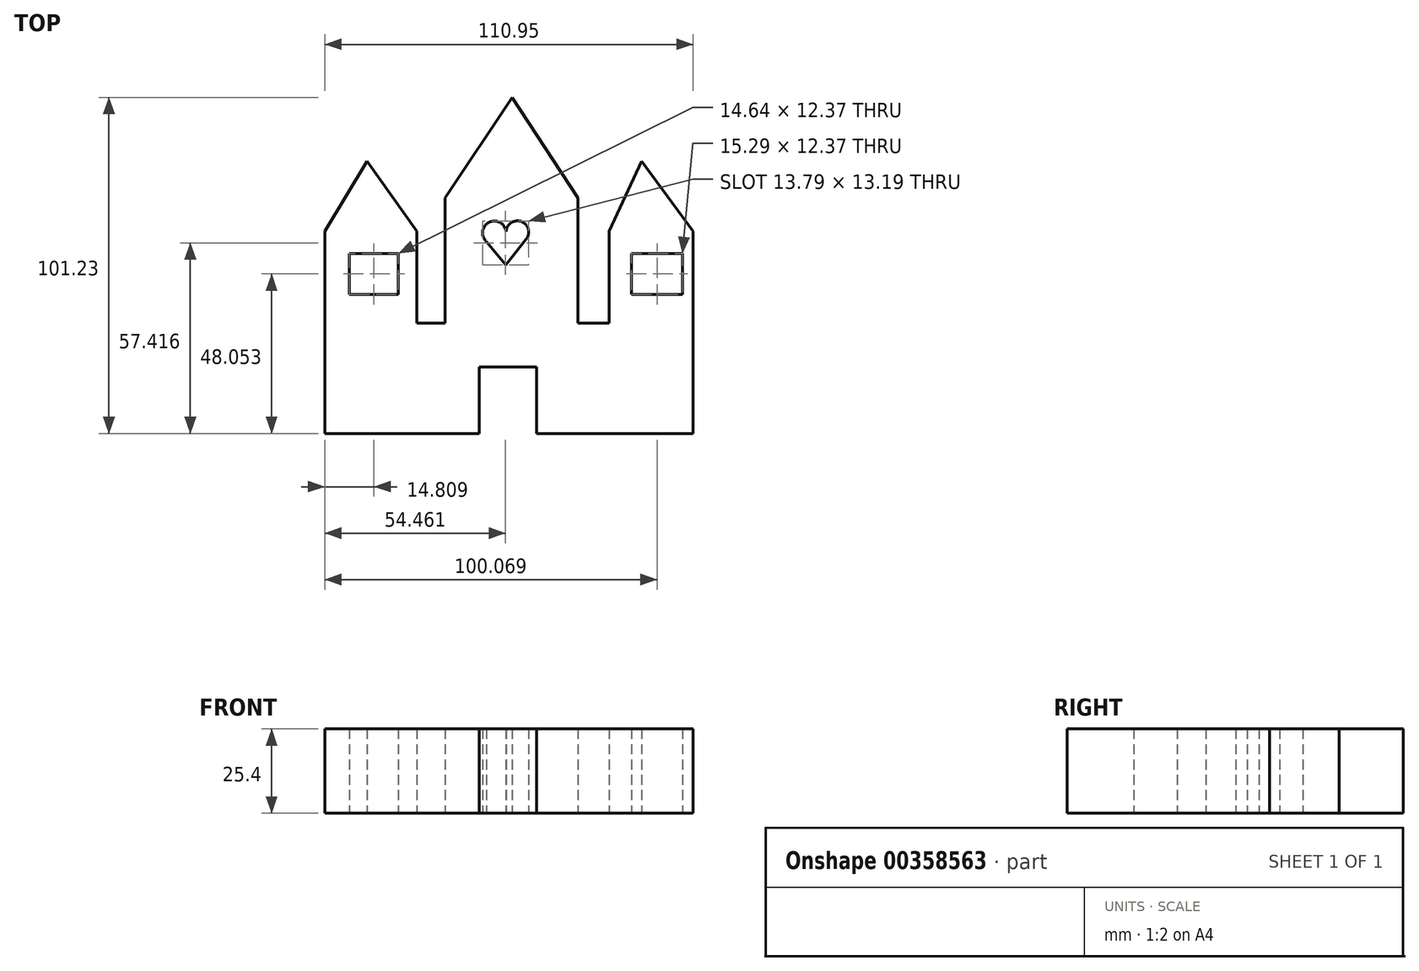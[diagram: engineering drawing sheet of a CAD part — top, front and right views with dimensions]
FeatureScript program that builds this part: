
annotation { "Feature Type Name" : "Feature", "Feature Type Description" : "" }
export const myFeature = defineFeature(function(context is Context, id is Id, definition is map)
    precondition{}
    {
        {
            var Q0;
            Q0=qCreatedBy(makeId("Top.planeOp"),FACE);
            var sketch = newSketch(context, id + "F0", { "sketchPlane" : qUnion([Q0])});
            skLineSegment(sketch, "E0.bottom", {"start": v(-8.53, -12.04) * mm, "end": v(0, -12.04) * mm});
            skLineSegment(sketch, "E0.top", {"start": v(-36.27, -45.26) * mm, "end": v(74.68, -45.26) * mm});
            skLineSegment(sketch, "E0.left", {"start": v(-36.27, -12.04) * mm, "end": v(-36.27, -45.26) * mm});
            skLineSegment(sketch, "E0.right", {"start": v(74.68, -12.04) * mm, "end": v(74.68, -45.26) * mm});
            skLineSegment(sketch, "E1", {"start": v(-36.27, -12.04) * mm, "end": v(-36.27, 15.7) * mm});
            skLineSegment(sketch, "E2", {"start": v(-8.53, -12.04) * mm, "end": v(-8.53, 15.7) * mm});
            skLineSegment(sketch, "E3", {"start": v(74.68, -12.04) * mm, "end": v(74.68, 15.7) * mm});
            skLineSegment(sketch, "E4", {"start": v(49.38, -12.04) * mm, "end": v(49.38, 15.7) * mm});
            skLineSegment(sketch, "E5", {"start": v(-36.27, 15.7) * mm, "end": v(-23.47, 36.73) * mm});
            skLineSegment(sketch, "E6", {"start": v(-23.47, 36.73) * mm, "end": v(-8.53, 15.7) * mm});
            skLineSegment(sketch, "E7", {"start": v(49.38, 15.7) * mm, "end": v(59.13, 36.73) * mm});
            skLineSegment(sketch, "E8", {"start": v(59.13, 36.73) * mm, "end": v(74.68, 15.7) * mm});
            skLineSegment(sketch, "E9", {"start": v(0, 25.76) * mm, "end": v(0, -12.04) * mm});
            skLineSegment(sketch, "E10", {"start": v(39.93, -12.04) * mm, "end": v(39.93, 25.76) * mm});
            skLineSegment(sketch, "E11", {"start": v(0, 25.76) * mm, "end": v(20.23, 55.97) * mm});
            skLineSegment(sketch, "E12", {"start": v(20.23, 55.97) * mm, "end": v(39.93, 25.76) * mm});
            skLineSegment(sketch, "E13.bottom", {"start": v(-28.78, 8.98) * mm, "end": v(-14.14, 8.98) * mm});
            skLineSegment(sketch, "E13.top", {"start": v(-28.78, -3.39) * mm, "end": v(-14.14, -3.39) * mm});
            skLineSegment(sketch, "E13.left", {"start": v(-28.78, 8.98) * mm, "end": v(-28.78, -3.39) * mm});
            skLineSegment(sketch, "E13.right", {"start": v(-14.14, 8.98) * mm, "end": v(-14.14, -3.39) * mm});
            skLineSegment(sketch, "E14.bottom", {"start": v(56.15, 8.98) * mm, "end": v(71.45, 8.98) * mm});
            skLineSegment(sketch, "E14.top", {"start": v(56.15, -3.39) * mm, "end": v(71.45, -3.39) * mm});
            skLineSegment(sketch, "E14.left", {"start": v(56.15, 8.98) * mm, "end": v(56.15, -3.39) * mm});
            skLineSegment(sketch, "E14.right", {"start": v(71.45, 8.98) * mm, "end": v(71.45, -3.39) * mm});
            skLineSegment(sketch, "E15.bottom", {"start": v(10.27, -25.2) * mm, "end": v(27.51, -25.2) * mm});
            skLineSegment(sketch, "E15.top", {"start": v(10.27, -45.26) * mm, "end": v(27.51, -45.26) * mm});
            skLineSegment(sketch, "E15.left", {"start": v(10.27, -25.2) * mm, "end": v(10.27, -45.26) * mm});
            skLineSegment(sketch, "E15.right", {"start": v(27.51, -25.2) * mm, "end": v(27.51, -45.26) * mm});
            skLineSegment(sketch, "E16.trimOffspring", {"start": v(39.93, -12.04) * mm, "end": v(49.38, -12.04) * mm});
            skPoint(sketch, "E17.center.orphan", {"position": v(23.94, 15.16) * mm});
            skPoint(sketch, "E18.center.orphan", {"position": v(14.82, 15.16) * mm});
            skPoint(sketch, "E19.start.orphan", {"position": v(20.03, 0) * mm});
            skArc(sketch, "E20", {"start": v(18.37, 15.48) * mm, "mid": v(13.21, 18.33) * mm, "end": v(12.47, 12.49) * mm});
            skArc(sketch, "E21", {"start": v(24.42, 13.26) * mm, "mid": v(22.93, 18.57) * mm, "end": v(18.37, 15.48) * mm});
            skLineSegment(sketch, "E22", {"start": v(11.78, 13.32) * mm, "end": v(18.27, 5.56) * mm});
            skLineSegment(sketch, "E23", {"start": v(18.27, 5.56) * mm, "end": v(24.42, 13.26) * mm});
            skSolve(sketch);
        }
        {
            var Q0;
            Q0=makeQuery(id+"F0.imprint","IMPRINT",FACE,{"disambiguationData":[TD([[makeQuery(id+"F0.imprint","IMPRINT",EDGE,{"derivedFrom":sQuery(id+"F0.wireOp",EDGE,"E0.bottom")}),-1.0]])]});
            extrude(context, id + "F1", {"entities" : qUnion([Q0]), "depth" : 25.4 * mm});
        }
    });
